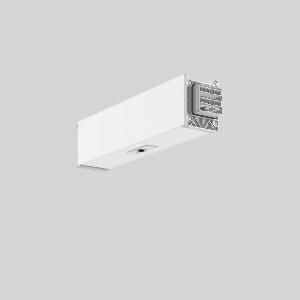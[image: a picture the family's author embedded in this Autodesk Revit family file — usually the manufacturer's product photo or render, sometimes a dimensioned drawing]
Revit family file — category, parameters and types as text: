
# Revit family: linedo_sensormodule_2-5_m_9503s1_002_700_000_ad4f
name_source: partatom
category: Lighting Fixtures
units: mm (PartAtom-declared; Revit-internal decimal feet)

## family parameters
Cut with Voids When Loaded = No
Host = Face
Light Source = No
Part Type = Normal
Room Calculation Point = No
Round Connector Dimension = Use Diameter
Shared = No

## types (1)
- LINEDO Sensormodule 2-5 m
    Apparent Load = 0 VA
    Default Elevation = 1800 mm
    Description = Series: LINEDO
Module including Passive Infrared (PIR) sensor for movement and ambient light. System profile made of aluminium extrusion profile, powder-coated. Simple, tool-free installation of system profiles using separate accessories for cable, chain or ceiling suspension. Tool-free connection and mechanical connectors to secure. 7-poles LINEDO connector (5 x 2.5 mm² / 2 x 1.5 mm²). Phase can be set via patended bridge without opening the luminaire. Pre-assembled connector for DALI line. Light and movement sensor: Housing of non-flammable, halogen-free plastic (polycarbonate). Presence detection with passive IR element. Presence detection range adjustable via integrated shutters between 40° and 90°. Detection range: 6 m. Light sensor range: 20-800 lx (measured at the sensor). Function display with two-colour LED. Installation height: 2-5 m. Example of use: Monitoring of low ceiling rooms and rack storage where the installation height is normal. Please order supply module, connection and mounting accessories separately. 
Colour: traffic white, matt (RAL 9016)
Length: 330 mm
Width: 58 mm
Height: 76 mm
Weight: 745 g
Type of Installation: Recessed mounting
    Height = 77 mm
    Lamp = 0 x
    Length = 331 mm
    Luminous efficacy = 0 lm/W
    Manufacturer = RZB
    ModVariant = No
    Model = 9503S1.002.700.000
    Mounting Place = Ceiling
    Mounting Type = Surface mounted, Pendant
    Number of Poles = 1
    OnlyDefault = Yes
    Power Factor = 1
    Product Name = LINEDO Sensormodule 2-5 m
    Product group = Surface mounted continuous line luminaire system
    ProductGroupID = 310
    Protection Class = Protection class I
    Protection Degree = IP 20
    RLX_Detail_Level = 1
    RLX_Emergency_Light_Flux = 0 lm
    RLX_Emergency_Type = 0
    RLX_Emergency_Type_DB = No
    RlxData = <blob elided: 21677 chars, md5=9941b782>
    Standby Power = 0 W
    System Light Flux = 0 lm
    System Power = 0 W
    Type Comments = Product without accessories
    Type Image = 9503s1.002.400.000.jpg
    URL = http://relux.com
    VarID = ---
    Voltage = 230 V
    Voltage Range = 220-240 V
    Weight = 0.00 kg
    Width = 58 mm

## geometry (parser evidence)
native form markers: Blend x4, Sweep x11
no freeform markers — native parametric forms only
